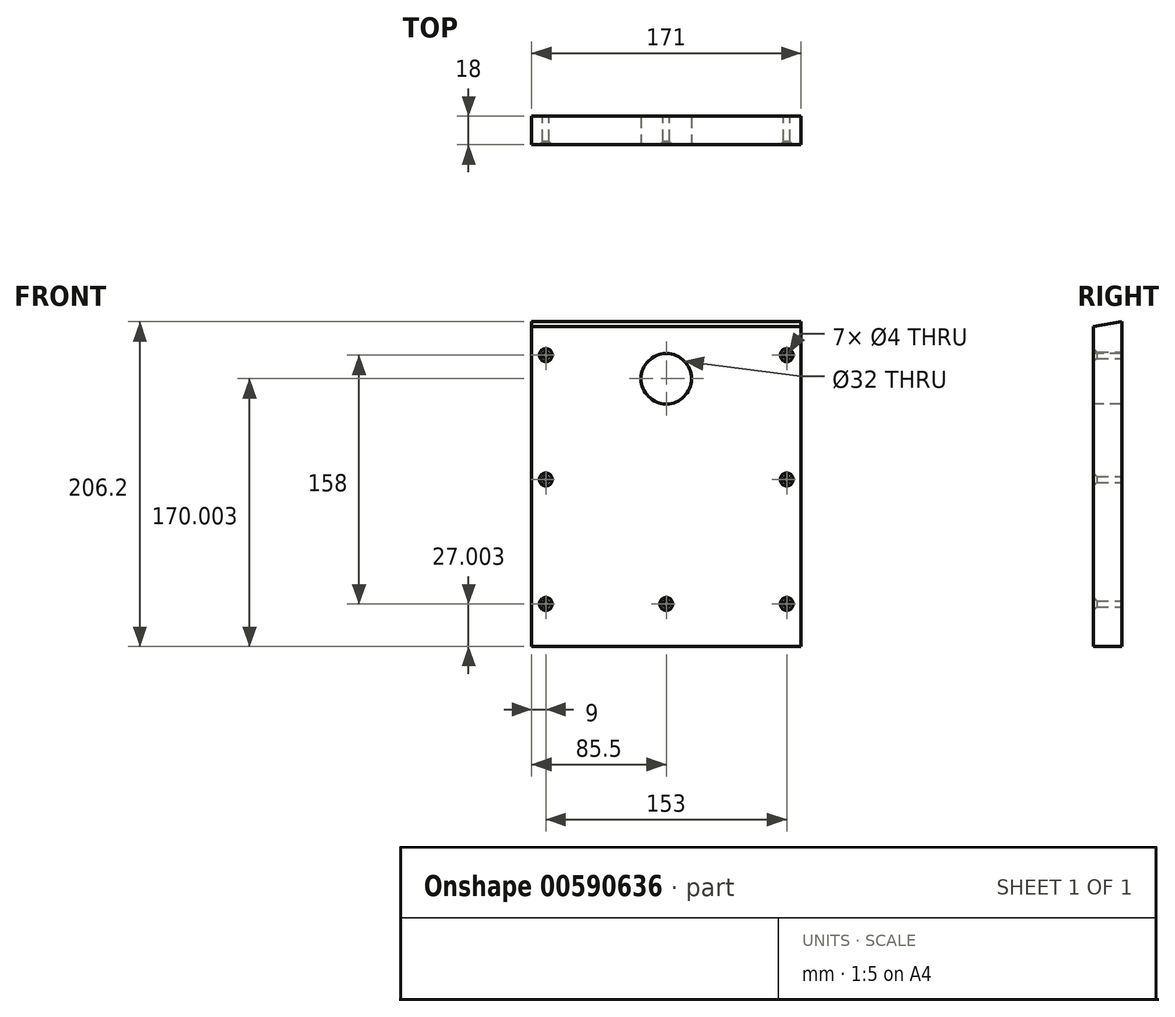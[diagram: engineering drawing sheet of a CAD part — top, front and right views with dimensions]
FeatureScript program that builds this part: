
annotation { "Feature Type Name" : "Feature", "Feature Type Description" : "" }
export const myFeature = defineFeature(function(context is Context, id is Id, definition is map)
    precondition{}
    {
        {
            var Q0;
            Q0=qCreatedBy(makeId("Front.planeOp"),FACE);
            var sketch = newSketch(context, id + "F0", { "sketchPlane" : qUnion([Q0])});
            skLineSegment(sketch, "E0.bottom", {"start": v(85.5, -103.1) * mm, "end": v(-85.5, -103.1) * mm});
            skLineSegment(sketch, "E0.top", {"start": v(85.5, 103.1) * mm, "end": v(-85.5, 103.1) * mm});
            skLineSegment(sketch, "E0.left", {"start": v(85.5, -103.1) * mm, "end": v(85.5, 103.1) * mm});
            skLineSegment(sketch, "E0.right", {"start": v(-85.5, -103.1) * mm, "end": v(-85.5, 103.1) * mm});
            skPoint(sketch, "E0.middle", {"position": v(0, 0) * mm});
            skPoint(sketch, "E1", {"position": v(0, 66.9) * mm});
            skSolve(sketch);
        }
        {
            var Q0;
            Q0=makeQuery(id+"F0.imprint","IMPRINT",FACE,{"disambiguationData":[TD([[makeQuery(id+"F0.imprint","IMPRINT",EDGE,{"derivedFrom":sQuery(id+"F0.wireOp",EDGE,"E0.bottom")}),-1.0]])]});
            extrude(context, id + "F1", {"entities" : qUnion([Q0]), "depth" : 18 * mm, "offsetDistance" : 25 * mm});
        }
        {
            var Q0;
            Q0=sQuery(id+"F0.wireOp",VERTEX,"E1");
            var Q1;
            Q1=makeQuery(id+"F1.opExtrude","SWEPT_BODY",BODY,{"disambiguationData":[OSD([sQuery(id+"F0.wireOp",EDGE,"E0.bottom"),sQuery(id+"F0.wireOp",EDGE,"E0.top"),sQuery(id+"F0.wireOp",EDGE,"E0.left"),sQuery(id+"F0.wireOp",EDGE,"E0.right")])]});
            hole(context, id + "F2", {"style" : HoleStyle.SIMPLE, "endStyle" : HoleEndStyle.THROUGH, "oppositeDirection" : true, "holeDiameter" : 32 * mm, "majorDiameter" : 5 * mm, "isTappedThrough" : true, "tappedDepth" : 12 * mm, "tapClearance" : 3, "locations" : qUnion([Q0]), "scope" : qUnion([Q1])});
        }
        {
            var Q0;
            Q0=makeQuery(id+"F1.opExtrude","SWEPT_FACE",FACE,{"disambiguationData":[OSD([sQuery(id+"F0.wireOp",EDGE,"E0.right")])]});
            var sketch = newSketch(context, id + "F3", { "sketchPlane" : qUnion([Q0])});
            skLineSegment(sketch, "E2", {"start": v(0, 103.1) * mm, "end": v(18, 99.92) * mm});
            skLineSegment(sketch, "E3", {"start": v(0, 103.1) * mm, "end": v(18, 103.1) * mm});
            skLineSegment(sketch, "E4", {"start": v(18, 103.1) * mm, "end": v(18, 99.92) * mm});
            skSolve(sketch);
        }
        {
            var Q0;
            Q0=makeQuery(id+"F3.imprint","IMPRINT",FACE,{"disambiguationData":[TD([[makeQuery(id+"F3.imprint","IMPRINT",EDGE,{"derivedFrom":sQuery(id+"F3.wireOp",EDGE,"E2")}),1.0]])]});
            extrude(context, id + "F4", {"entities" : qUnion([Q0]), "operationType" : NewBodyOperationType.REMOVE, "endBound" : BoundingType.THROUGH_ALL, "oppositeDirection" : true, "depth" : 25 * mm, "offsetDistance" : 25 * mm});
        }
        {
            var Q0;
            Q0=makeQuery(id+"F1.opExtrude","CAP_FACE",FACE,{"disambiguationData":[OSD([sQuery(id+"F0.wireOp",EDGE,"E0.bottom"),sQuery(id+"F0.wireOp",EDGE,"E0.top"),sQuery(id+"F0.wireOp",EDGE,"E0.left"),sQuery(id+"F0.wireOp",EDGE,"E0.right")])],"isStart":false});
            var sketch = newSketch(context, id + "F5", { "sketchPlane" : qUnion([Q0])});
            skPoint(sketch, "E5", {"position": v(0, -76.1) * mm});
            skPoint(sketch, "E6", {"position": v(-76.5, -76.1) * mm});
            skPoint(sketch, "E7", {"position": v(76.5, -76.1) * mm});
            skPoint(sketch, "E8", {"position": v(76.5, 81.9) * mm});
            skPoint(sketch, "E9", {"position": v(-76.5, 81.9) * mm});
            skPoint(sketch, "E10", {"position": v(-76.5, 2.9) * mm});
            skPoint(sketch, "E11", {"position": v(76.5, 2.9) * mm});
            skSolve(sketch);
        }
        {
            var Q0;
            Q0=sQuery(id+"F5.wireOp",VERTEX,"E5");
            var Q1;
            Q1=makeQuery(id+"F1.opExtrude","SWEPT_BODY",BODY,{"disambiguationData":[OSD([sQuery(id+"F0.wireOp",EDGE,"E0.bottom"),sQuery(id+"F0.wireOp",EDGE,"E0.top"),sQuery(id+"F0.wireOp",EDGE,"E0.left"),sQuery(id+"F0.wireOp",EDGE,"E0.right")])]});
            hole(context, id + "F6", {"style" : HoleStyle.C_SINK, "endStyle" : HoleEndStyle.THROUGH, "holeDiameter" : 4 * mm, "cSinkDiameter" : 8.2 * mm, "cSinkAngle" : 90 * degree, "majorDiameter" : 5 * mm, "isTappedThrough" : true, "tappedDepth" : 12 * mm, "tapClearance" : 3, "locations" : qUnion([Q0]), "scope" : qUnion([Q1])});
        }
        {
            var Q0;
            Q0=sQuery(id+"F5.wireOp",VERTEX,"E6");
            var Q1;
            Q1=sQuery(id+"F5.wireOp",VERTEX,"E7");
            var Q2;
            Q2=makeQuery(id+"F1.opExtrude","SWEPT_BODY",BODY,{"disambiguationData":[OSD([sQuery(id+"F0.wireOp",EDGE,"E0.bottom"),sQuery(id+"F0.wireOp",EDGE,"E0.top"),sQuery(id+"F0.wireOp",EDGE,"E0.left"),sQuery(id+"F0.wireOp",EDGE,"E0.right")])]});
            hole(context, id + "F7", {"style" : HoleStyle.C_SINK, "endStyle" : HoleEndStyle.THROUGH, "holeDiameter" : 4 * mm, "cSinkDiameter" : 8.2 * mm, "cSinkAngle" : 90 * degree, "majorDiameter" : 5 * mm, "isTappedThrough" : true, "tappedDepth" : 12 * mm, "tapClearance" : 3, "locations" : qUnion([Q0, Q1]), "scope" : qUnion([Q2])});
        }
        {
            var Q0;
            Q0=sQuery(id+"F5.wireOp",VERTEX,"E9");
            var Q1;
            Q1=sQuery(id+"F5.wireOp",VERTEX,"E8");
            var Q2;
            Q2=makeQuery(id+"F1.opExtrude","SWEPT_BODY",BODY,{"disambiguationData":[OSD([sQuery(id+"F0.wireOp",EDGE,"E0.bottom"),sQuery(id+"F0.wireOp",EDGE,"E0.top"),sQuery(id+"F0.wireOp",EDGE,"E0.left"),sQuery(id+"F0.wireOp",EDGE,"E0.right")])]});
            hole(context, id + "F8", {"style" : HoleStyle.C_SINK, "endStyle" : HoleEndStyle.THROUGH, "holeDiameter" : 4 * mm, "cSinkDiameter" : 8.2 * mm, "cSinkAngle" : 90 * degree, "majorDiameter" : 5 * mm, "isTappedThrough" : true, "tappedDepth" : 12 * mm, "tapClearance" : 3, "locations" : qUnion([Q0, Q1]), "scope" : qUnion([Q2])});
        }
        {
            var Q0;
            Q0=sQuery(id+"F5.wireOp",VERTEX,"E10");
            var Q1;
            Q1=sQuery(id+"F5.wireOp",VERTEX,"E11");
            var Q2;
            Q2=makeQuery(id+"F1.opExtrude","SWEPT_BODY",BODY,{"disambiguationData":[OSD([sQuery(id+"F0.wireOp",EDGE,"E0.bottom"),sQuery(id+"F0.wireOp",EDGE,"E0.top"),sQuery(id+"F0.wireOp",EDGE,"E0.left"),sQuery(id+"F0.wireOp",EDGE,"E0.right")])]});
            hole(context, id + "F9", {"style" : HoleStyle.C_SINK, "endStyle" : HoleEndStyle.THROUGH, "holeDiameter" : 4 * mm, "cSinkDiameter" : 8.2 * mm, "cSinkAngle" : 90 * degree, "majorDiameter" : 5 * mm, "isTappedThrough" : true, "tappedDepth" : 12 * mm, "tapClearance" : 3, "locations" : qUnion([Q0, Q1]), "scope" : qUnion([Q2])});
        }
    });
